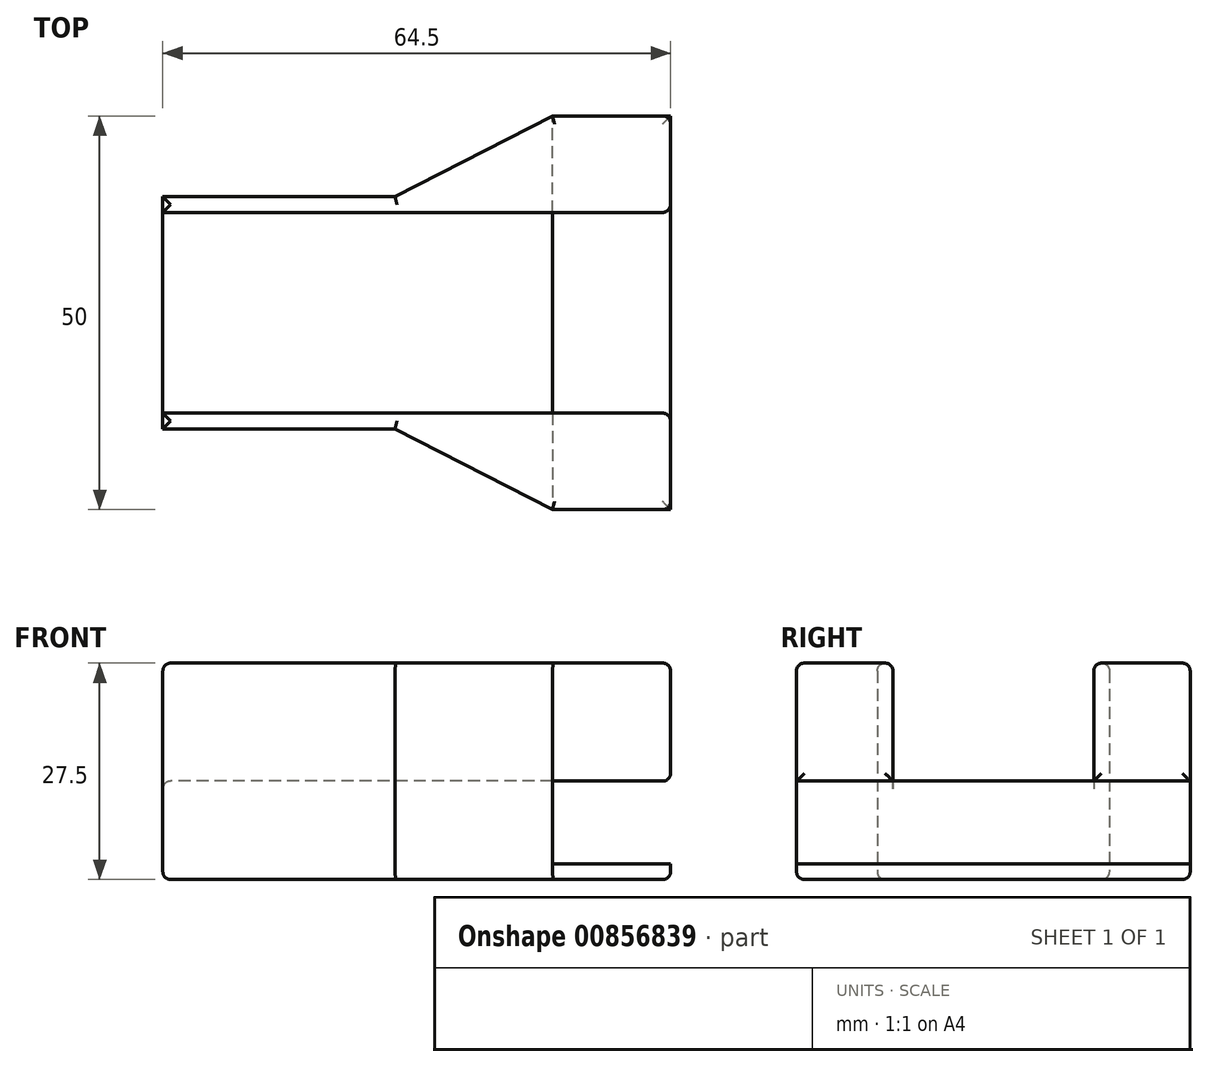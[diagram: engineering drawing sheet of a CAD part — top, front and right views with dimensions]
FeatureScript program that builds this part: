
annotation { "Feature Type Name" : "Feature", "Feature Type Description" : "" }
export const myFeature = defineFeature(function(context is Context, id is Id, definition is map)
    precondition{}
    {
        {
            var Q0;
            Q0=qCreatedBy(makeId("Top.planeOp"),FACE);
            var sketch = newSketch(context, id + "F0", { "sketchPlane" : qUnion([Q0])});
            skLineSegment(sketch, "E0.bottom", {"start": v(0, 0) * mm, "end": v(-29.5, 0) * mm});
            skLineSegment(sketch, "E0.top", {"start": v(0, -14.75) * mm, "end": v(-29.5, -14.75) * mm});
            skLineSegment(sketch, "E0.left", {"start": v(0, 0) * mm, "end": v(0, -12.75) * mm});
            skLineSegment(sketch, "E0.right", {"start": v(-29.5, 0) * mm, "end": v(-29.5, -14.75) * mm});
            skLineSegment(sketch, "E1.bottom", {"start": v(20, 0) * mm, "end": v(35, 0) * mm});
            skLineSegment(sketch, "E1.top", {"start": v(20, -25) * mm, "end": v(35, -25) * mm});
            skLineSegment(sketch, "E1.left", {"start": v(20, 0) * mm, "end": v(20, -25) * mm});
            skLineSegment(sketch, "E1.right", {"start": v(35, 0) * mm, "end": v(35, -25) * mm});
            skLineSegment(sketch, "E2", {"start": v(20, 0) * mm, "end": v(0, 0) * mm});
            skLineSegment(sketch, "E3", {"start": v(0, -14.75) * mm, "end": v(20, -25) * mm});
            skLineSegment(sketch, "E4", {"start": v(-29.5, -12.75) * mm, "end": v(35, -12.75) * mm});
            skPoint(sketch, "E4.endSnap0", {"position": v(35, -12.5) * mm});
            skSolve(sketch);
        }
        {
            var Q0;
            {var subQ0=sQuery(id+"F0.wireOp",EDGE,"E0.bottom");Q0=makeQuery(id+"F0.imprint","IMPRINT",FACE,{"disambiguationData":[TD([[makeQuery(id+"F0.imprint","IMPRINT",EDGE,{"derivedFrom":subQ0}),1.0]])]});}
            var Q1;
            {var subQ5=sQuery(id+"F0.wireOp",EDGE,"E0.top");Q1=makeQuery(id+"F0.imprint","IMPRINT",FACE,{"disambiguationData":[TD([[makeQuery(id+"F0.imprint","IMPRINT",EDGE,{"derivedFrom":subQ5}),-1.0]])]});}
            var Q2;
            Q2=makeQuery(id+"F0.imprint","IMPRINT",FACE,{"disambiguationData":[TD([[makeQuery(id+"F0.imprint","IMPRINT",EDGE,{"derivedFrom":sQuery(id+"F0.wireOp",EDGE,"E0.left")}),1.0]])]});
            var Q3;
            {var subQ3=sQuery(id+"F0.wireOp",EDGE,"E1.bottom");Q3=makeQuery(id+"F0.imprint","IMPRINT",FACE,{"disambiguationData":[TD([[makeQuery(id+"F0.imprint","IMPRINT",EDGE,{"derivedFrom":subQ3}),-1.0]])]});}
            var Q4;
            {var subQ0=sQuery(id+"F0.wireOp",EDGE,"E1.top");Q4=makeQuery(id+"F0.imprint","IMPRINT",FACE,{"disambiguationData":[TD([[makeQuery(id+"F0.imprint","IMPRINT",EDGE,{"derivedFrom":subQ0}),1.0]])]});}
            extrude(context, id + "F1", {"entities" : qUnion([Q0, Q1, Q2, Q3, Q4]), "depth" : 12.5 * mm, "offsetDistance" : 25 * mm});
        }
        {
            var Q0;
            {var subQ1=sQuery(id+"F0.wireOp",EDGE,"E0.top");Q0=makeQuery(id+"F0.imprint","IMPRINT",FACE,{"disambiguationData":[TD([[makeQuery(id+"F0.imprint","IMPRINT",EDGE,{"derivedFrom":subQ1}),-1.0]])]});}
            var Q1;
            {var subQ0=sQuery(id+"F0.wireOp",EDGE,"E1.top");Q1=makeQuery(id+"F0.imprint","IMPRINT",FACE,{"disambiguationData":[TD([[makeQuery(id+"F0.imprint","IMPRINT",EDGE,{"derivedFrom":subQ0}),1.0]])]});}
            extrude(context, id + "F2", {"entities" : qUnion([Q0, Q1]), "operationType" : NewBodyOperationType.ADD, "depth" : 27.5 * mm, "offsetDistance" : 25 * mm});
        }
        {
            var Q0;
            {var subQ0=sQuery(id+"F0.wireOp",EDGE,"E1.right");Q0=makeQuery(id+"F2.boolean.opBoolean","MERGE",FACE,{"derivedFrom":[makeQuery(id+"F1.opExtrude","SWEPT_FACE",FACE,{"disambiguationData":[OSD([subQ0])]}),makeQuery(id+"F2.opExtrude","SWEPT_FACE",FACE,{"disambiguationData":[OSD([subQ0])]})]});}
            var sketch = newSketch(context, id + "F3", { "sketchPlane" : qUnion([Q0])});
            skLineSegment(sketch, "E5.bottom", {"start": v(0, 2) * mm, "end": v(-25, 2) * mm});
            skLineSegment(sketch, "E5.top", {"start": v(0, 12.5) * mm, "end": v(-25, 12.5) * mm});
            skLineSegment(sketch, "E5.left", {"start": v(0, 2) * mm, "end": v(0, 12.5) * mm});
            skLineSegment(sketch, "E5.right", {"start": v(-25, 2) * mm, "end": v(-25, 12.5) * mm});
            skSolve(sketch);
        }
        {
            var Q0;
            Q0=makeQuery(id+"F3.imprint","IMPRINT",FACE,{"disambiguationData":[TD([[makeQuery(id+"F3.imprint","IMPRINT",EDGE,{"derivedFrom":sQuery(id+"F3.wireOp",EDGE,"E5.bottom")}),-1.0]])]});
            extrude(context, id + "F4", {"entities" : qUnion([Q0]), "operationType" : NewBodyOperationType.REMOVE, "oppositeDirection" : true, "depth" : 15 * mm, "offsetDistance" : 25 * mm});
        }
        {
            var Q0;
            Q0=makeQuery(id+"F1.opExtrude","SWEPT_BODY",BODY,{"disambiguationData":[OSD([sQuery(id+"F0.wireOp",EDGE,"E0.bottom"),sQuery(id+"F0.wireOp",EDGE,"E0.top"),sQuery(id+"F0.wireOp",EDGE,"E0.right"),sQuery(id+"F0.wireOp",EDGE,"E1.bottom"),sQuery(id+"F0.wireOp",EDGE,"E1.top"),sQuery(id+"F0.wireOp",EDGE,"E1.right"),sQuery(id+"F0.wireOp",EDGE,"E2"),sQuery(id+"F0.wireOp",EDGE,"E3")])]});
            var Q1;
            Q1=qCreatedBy(makeId("Front.planeOp"),FACE);
            mirror(context, id + "F5", {"operationType" : NewBodyOperationType.ADD, "entities" : qUnion([Q0]), "mirrorPlane" : qUnion([Q1])});
        }
        {
            var Q0;
            {var subQ0=makeQuery(id+"F1.opExtrude","CAP_FACE",FACE,{"disambiguationData":[OSD([sQuery(id+"F0.wireOp",EDGE,"E0.bottom"),sQuery(id+"F0.wireOp",EDGE,"E0.top"),sQuery(id+"F0.wireOp",EDGE,"E0.right"),sQuery(id+"F0.wireOp",EDGE,"E1.bottom"),sQuery(id+"F0.wireOp",EDGE,"E1.top"),sQuery(id+"F0.wireOp",EDGE,"E1.right"),sQuery(id+"F0.wireOp",EDGE,"E2"),sQuery(id+"F0.wireOp",EDGE,"E3")])],"isStart":true});Q0=makeQuery(id+"F5.boolean.opBoolean","MERGE",FACE,{"derivedFrom":[subQ0,makeQuery(id+"F5.opPattern","COPY",FACE,{"derivedFrom":subQ0,"instanceName":"1"})]});}
            var Q1;
            Q1=makeQuery(id+"F2.opExtrude","CAP_FACE",FACE,{"disambiguationData":[OSD([sQuery(id+"F0.wireOp",EDGE,"E0.top"),sQuery(id+"F0.wireOp",EDGE,"E0.right"),sQuery(id+"F0.wireOp",EDGE,"E1.top"),sQuery(id+"F0.wireOp",EDGE,"E1.right"),sQuery(id+"F0.wireOp",EDGE,"E3"),sQuery(id+"F0.wireOp",EDGE,"E4")])],"isStart":false});
            var Q2;
            Q2=makeQuery(id+"F5.opPattern","COPY",FACE,{"derivedFrom":makeQuery(id+"F2.opExtrude","CAP_FACE",FACE,{"disambiguationData":[OSD([sQuery(id+"F0.wireOp",EDGE,"E0.top"),sQuery(id+"F0.wireOp",EDGE,"E0.right"),sQuery(id+"F0.wireOp",EDGE,"E1.top"),sQuery(id+"F0.wireOp",EDGE,"E1.right"),sQuery(id+"F0.wireOp",EDGE,"E3"),sQuery(id+"F0.wireOp",EDGE,"E4")])],"isStart":false}),"instanceName":"1"});
            var Q3;
            {var subQ0=sQuery(id+"F0.wireOp",EDGE,"E1.right");var subQ1=sQuery(id+"F0.wireOp",EDGE,"E1.top");Q3=makeQuery(id+"F5.opPattern","COPY",EDGE,{"derivedFrom":makeQuery(id+"F4.boolean.opBoolean","SPLIT",EDGE,{"disambiguationData":[TD([makeQuery(id+"F4.opExtrude","SWEPT_FACE",FACE,{"disambiguationData":[OSD([sQuery(id+"F3.wireOp",EDGE,"E5.top")])]})])],"derivedFrom":makeQuery(id+"F2.boolean.opBoolean","MERGE",EDGE,{"derivedFrom":[makeQuery(id+"F1.opExtrude","SWEPT_EDGE",EDGE,{"disambiguationData":[OSD([subQ1,subQ0])]}),makeQuery(id+"F2.opExtrude","SWEPT_EDGE",EDGE,{"disambiguationData":[OSD([subQ1,subQ0])]})]})}),"instanceName":"1"});}
            var Q4;
            {var subQ0=sQuery(id+"F0.wireOp",EDGE,"E4");var subQ1=sQuery(id+"F0.wireOp",EDGE,"E1.right");Q4=makeQuery(id+"F5.opPattern","COPY",FACE,{"derivedFrom":makeQuery(id+"F4.boolean.opBoolean","SPLIT",FACE,{"disambiguationData":[TD([makeQuery(id+"F2.opExtrude","SWEPT_FACE",FACE,{"disambiguationData":[OSD([subQ0])]})])],"derivedFrom":makeQuery(id+"F2.boolean.opBoolean","MERGE",FACE,{"derivedFrom":[makeQuery(id+"F1.opExtrude","SWEPT_FACE",FACE,{"disambiguationData":[OSD([subQ1])]}),makeQuery(id+"F2.opExtrude","SWEPT_FACE",FACE,{"disambiguationData":[OSD([subQ1])]})]})}),"instanceName":"1"});}
            var Q5;
            {var subQ0=sQuery(id+"F0.wireOp",EDGE,"E4");var subQ1=sQuery(id+"F0.wireOp",EDGE,"E1.right");Q5=makeQuery(id+"F4.boolean.opBoolean","SPLIT",FACE,{"disambiguationData":[TD([makeQuery(id+"F2.opExtrude","SWEPT_FACE",FACE,{"disambiguationData":[OSD([subQ0])]})])],"derivedFrom":makeQuery(id+"F2.boolean.opBoolean","MERGE",FACE,{"derivedFrom":[makeQuery(id+"F1.opExtrude","SWEPT_FACE",FACE,{"disambiguationData":[OSD([subQ1])]}),makeQuery(id+"F2.opExtrude","SWEPT_FACE",FACE,{"disambiguationData":[OSD([subQ1])]})]})});}
            var Q6;
            {var subQ0=makeQuery(id+"F1.opExtrude","CAP_EDGE",EDGE,{"disambiguationData":[OSD([sQuery(id+"F0.wireOp",EDGE,"E0.right")])],"isStart":false});Q6=makeQuery(id+"F5.boolean.opBoolean","MERGE",EDGE,{"derivedFrom":[subQ0,makeQuery(id+"F5.opPattern","COPY",EDGE,{"derivedFrom":subQ0,"instanceName":"1"})]});}
            fillet(context, id + "F6", {"entities" : qUnion([Q0, Q1, Q2, Q3, Q4, Q5, Q6]), "radius" : 1 * mm, "tangentPropagation" : true, "allowEdgeOverflow" : false});
        }
    });
